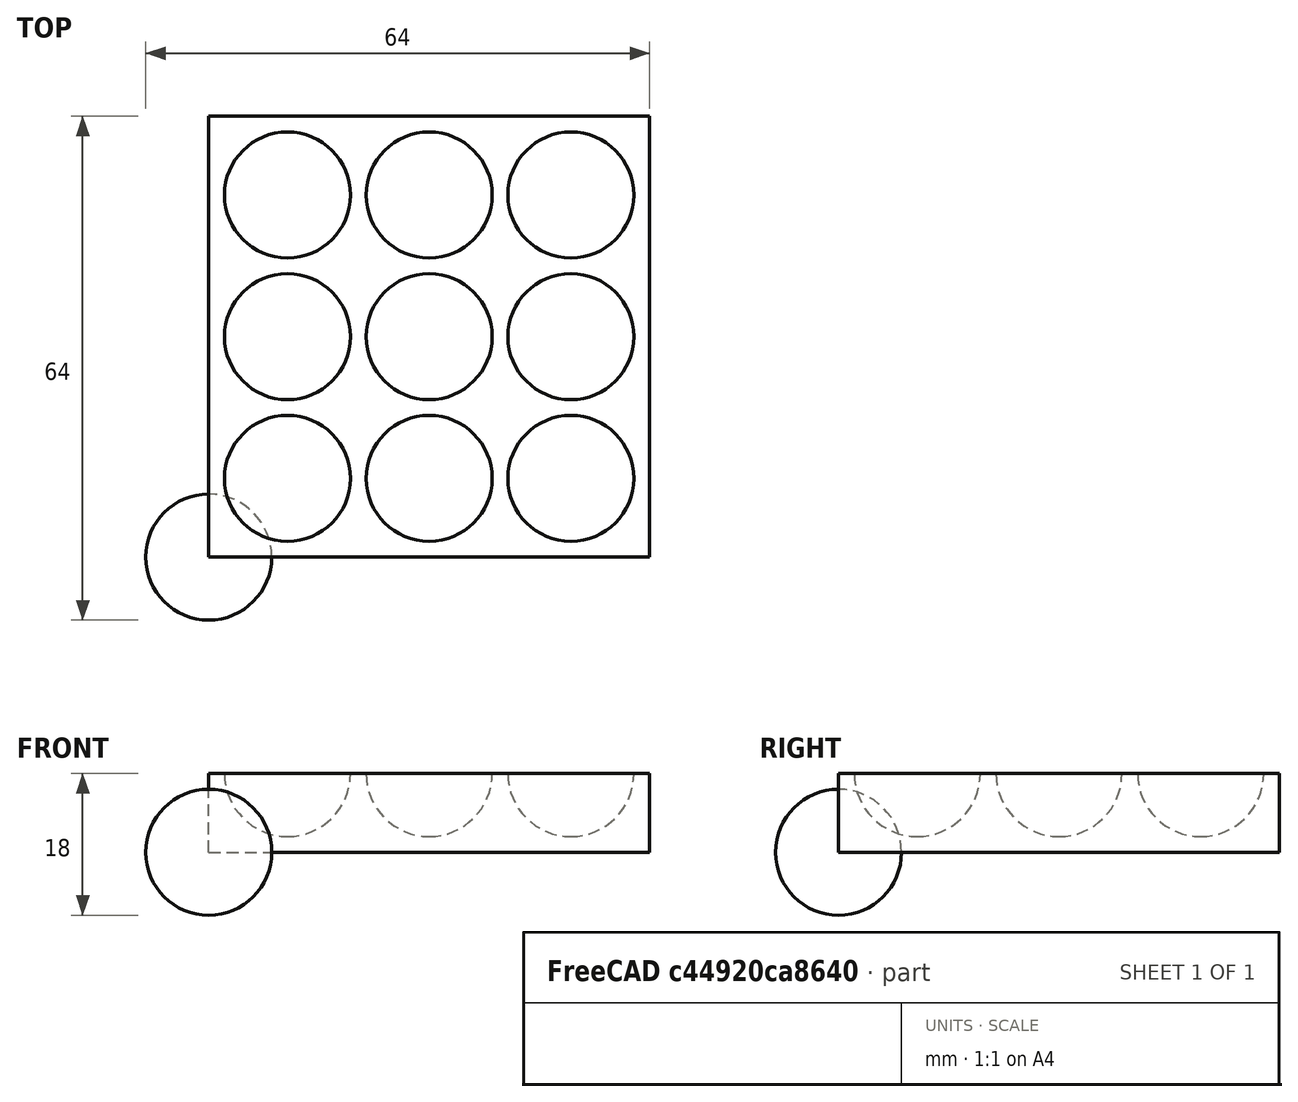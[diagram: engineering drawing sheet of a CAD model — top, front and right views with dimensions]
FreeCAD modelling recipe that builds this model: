
FCSTD DOCUMENT  (FreeCAD 1.0R39285 (Git))
Label: ojt1_t13p01_pheres
License: All rights reserved
objects: Part::Sphere×1, Part::FeaturePython×1, Part::Box×1, Part::Cut×1
note: 3 computed .brp shape members not serialized (recipe doc carries the construction recipe); baked Part::Feature solids carry a one-line shape summary decoded from their .brp

FEATURE [Part::Sphere] Sphere  label="Esfera"
  Angle1 = -90
  Angle2 = 90
  Angle3 = 360
  AttacherType = Attacher::AttachEngine3D
  Radius = 8
FEATURE [Part::FeaturePython] Array  # Draft array (typed FeaturePython)
  AlwaysSyncPlacement = false
  Angle = 360
  ArrayType = 0
  Axis = (0,0,1)
  Base = -> Sphere
  Center = (0,0,0)
  Count = 9
  ExpandArray = false
  Fuse = false
  IntervalAxis = (0,0,0)
  IntervalX = (18,0,0)
  IntervalY = (0,18,0)
  IntervalZ = (0,0,100)
  NumberCircles = 3
  NumberPolar = 5
  NumberX = 3
  NumberY = 3
  NumberZ = 1
  Placement = pos=(10,10,10) rot=(0,0,1;0rad)
  PlacementList = 9 placements: [(0,0,0),(0,18,0),(0,36,0),(18,0,0),(18,18,0),(18,36,0),(36,0,0),(36,18,0),(36,36,0)]
  RadialDistance = 50
  ScaleList = (9) [(1,1,1),(1,1,1),(1,1,1),(1,1,1),(1,1,1),(1,1,1),(1,1,1),(1,1,1),(1,1,1)]
  Symmetry = 1
  TangentialDistance = 25
FEATURE [Part::Box] Box  label="Cub"
  AttacherType = Attacher::AttachEngine3D
  Height = 10
  Length = 56
  Width = 56
FEATURE [Part::Cut] Cut
  Base = -> Box
  Refine = true
  Tool = -> Array
